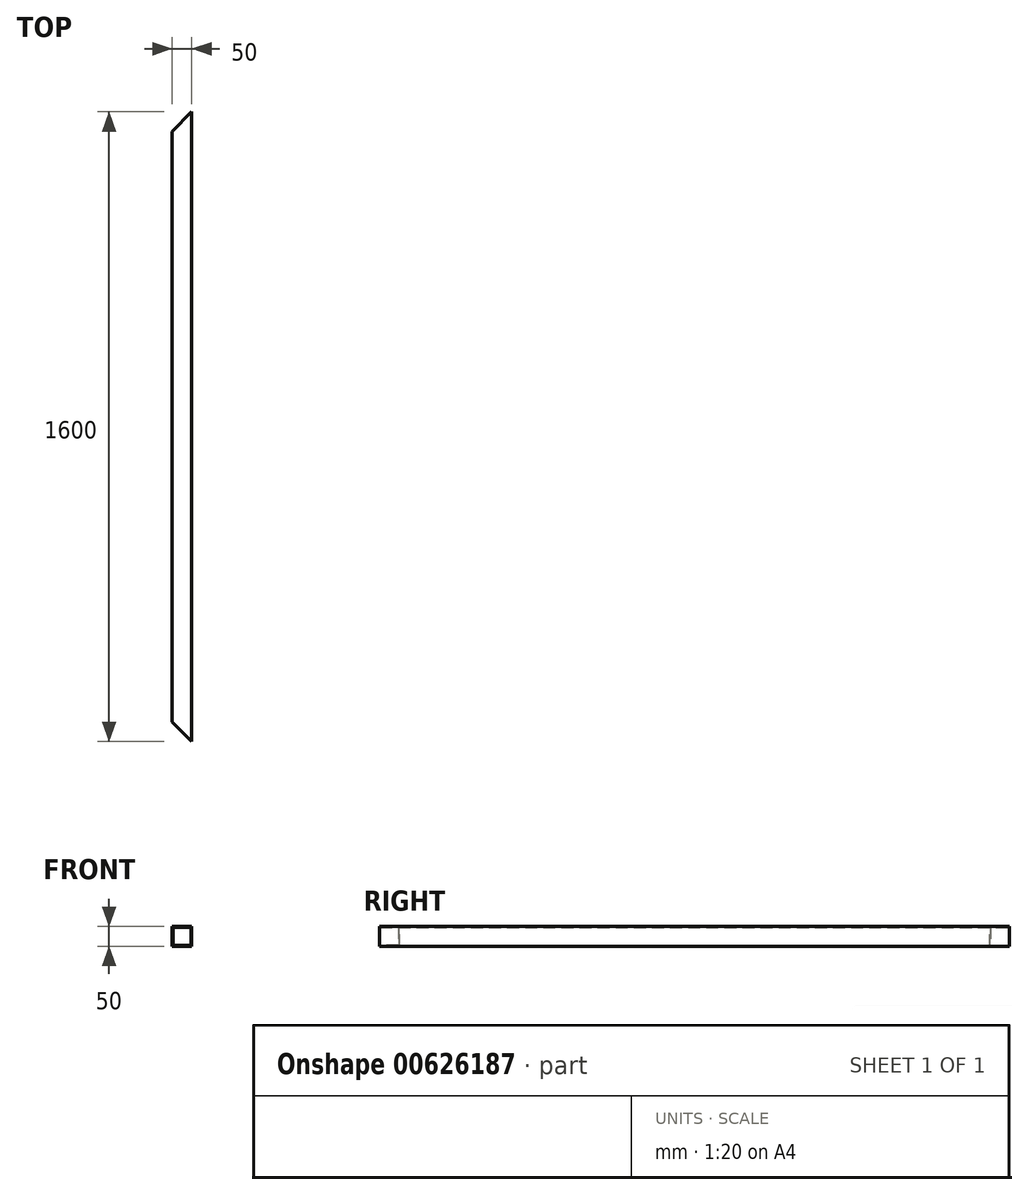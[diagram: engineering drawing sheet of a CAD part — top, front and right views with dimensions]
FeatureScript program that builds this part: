
annotation { "Feature Type Name" : "Feature", "Feature Type Description" : "" }
export const myFeature = defineFeature(function(context is Context, id is Id, definition is map)
    precondition{}
    {
        {
            var Q0;
            Q0=qCreatedBy(makeId("Front.planeOp"),FACE);
            var sketch = newSketch(context, id + "F0", { "sketchPlane" : qUnion([Q0])});
            skLineSegment(sketch, "E0", {"start": v(0, 0) * mm, "end": v(50, 0) * mm});
            skLineSegment(sketch, "E1", {"start": v(50, 0) * mm, "end": v(50, 50) * mm});
            skLineSegment(sketch, "E2", {"start": v(50, 50) * mm, "end": v(0, 50) * mm});
            skLineSegment(sketch, "E3", {"start": v(0, 50) * mm, "end": v(0, 0) * mm});
            skLineSegment(sketch, "E4.0", {"start": v(48, 48) * mm, "end": v(2, 48) * mm});
            skLineSegment(sketch, "E5.0", {"start": v(48, 2) * mm, "end": v(48, 48) * mm});
            skLineSegment(sketch, "E6.0", {"start": v(2, 48) * mm, "end": v(2, 2) * mm});
            skLineSegment(sketch, "E7.0", {"start": v(2, 2) * mm, "end": v(48, 2) * mm});
            skSolve(sketch);
        }
        {
            var Q0;
            {var subQ0=sQuery(id+"F0.wireOp",EDGE,"E2");Q0=makeQuery(id+"F0.imprint","IMPRINT",FACE,{"disambiguationData":[TD([[makeQuery(id+"F0.imprint","IMPRINT",EDGE,{"derivedFrom":subQ0}),1.0]])]});}
            extrude(context, id + "F1", {"entities" : qUnion([Q0]), "depth" : 1600 * mm, "offsetDistance" : 25 * mm});
        }
        {
            var Q0;
            Q0=makeQuery(id+"F1.opExtrude","SWEPT_FACE",FACE,{"disambiguationData":[OSD([sQuery(id+"F0.wireOp",EDGE,"E2")])]});
            var sketch = newSketch(context, id + "F2", { "sketchPlane" : qUnion([Q0])});
            skLineSegment(sketch, "E8", {"start": v(0, 0) * mm, "end": v(0, -50) * mm});
            skLineSegment(sketch, "E9", {"start": v(0, -50) * mm, "end": v(50, 0) * mm});
            skLineSegment(sketch, "E10", {"start": v(50, 0) * mm, "end": v(0, 0) * mm});
            skLineSegment(sketch, "E11", {"start": v(0, -1600) * mm, "end": v(0, -1550) * mm});
            skLineSegment(sketch, "E12", {"start": v(0, -1550) * mm, "end": v(50, -1600) * mm});
            skLineSegment(sketch, "E13", {"start": v(50, -1600) * mm, "end": v(0, -1600) * mm});
            skSolve(sketch);
        }
        {
            var Q0;
            Q0=makeQuery(id+"F2.imprint","IMPRINT",FACE,{"disambiguationData":[TD([[makeQuery(id+"F2.imprint","IMPRINT",EDGE,{"derivedFrom":sQuery(id+"F2.wireOp",EDGE,"E8")}),-1.0]])]});
            extrude(context, id + "F3", {"entities" : qUnion([Q0]), "operationType" : NewBodyOperationType.REMOVE, "oppositeDirection" : true, "depth" : 50 * mm, "offsetDistance" : 25 * mm});
        }
        {
            var Q0;
            Q0=qSketchRegion(id+"F2",true);
            extrude(context, id + "F4", {"entities" : qUnion([Q0]), "operationType" : NewBodyOperationType.REMOVE, "oppositeDirection" : true, "depth" : 50 * mm, "offsetDistance" : 25 * mm});
        }
    });
